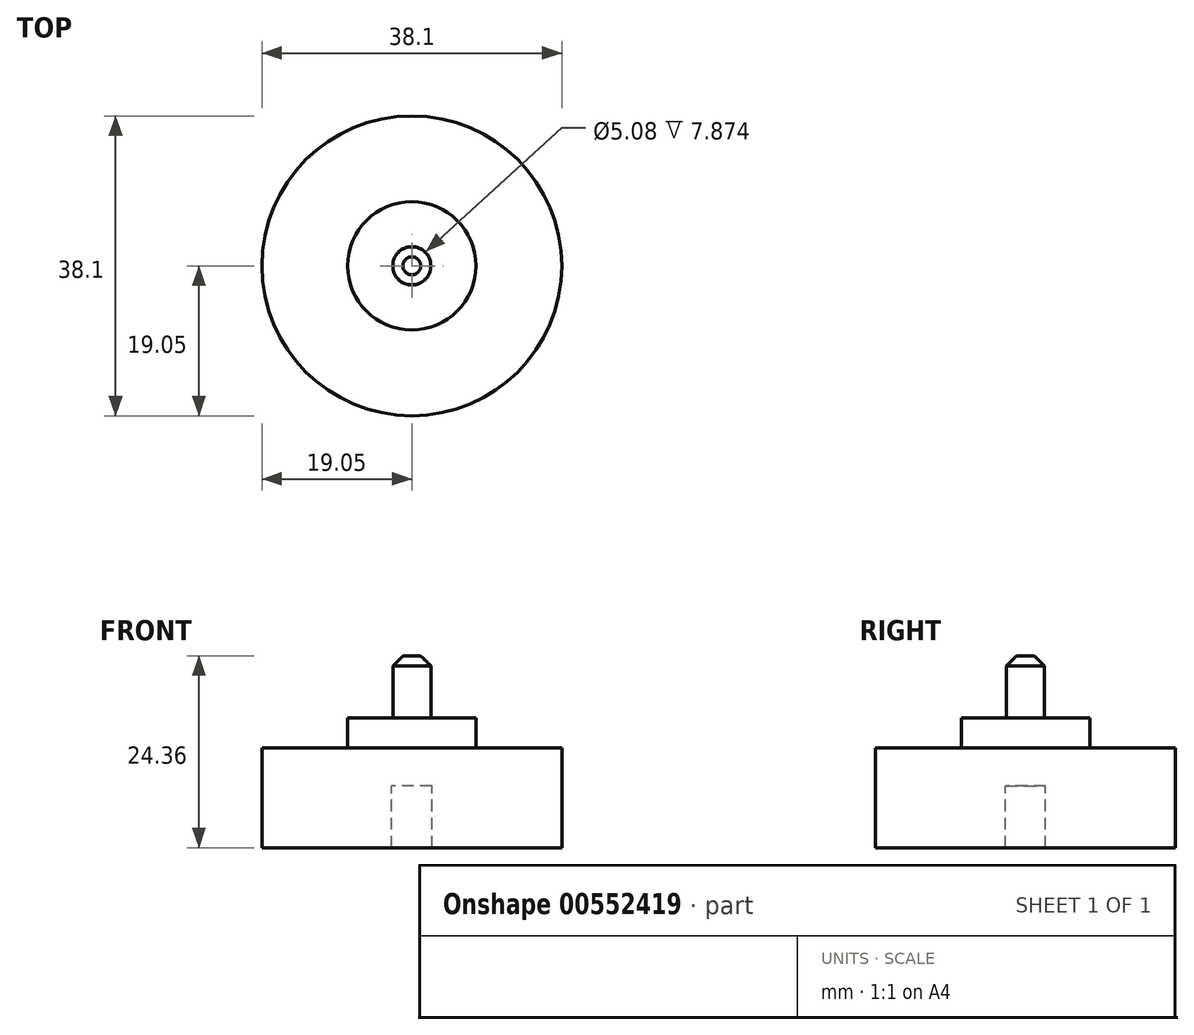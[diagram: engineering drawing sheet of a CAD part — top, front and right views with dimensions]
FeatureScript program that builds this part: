
annotation { "Feature Type Name" : "Feature", "Feature Type Description" : "" }
export const myFeature = defineFeature(function(context is Context, id is Id, definition is map)
    precondition{}
    {
        {
            var Q0;
            Q0=qCreatedBy(makeId("Front.planeOp"),FACE);
            var sketch = newSketch(context, id + "F0", { "sketchPlane" : qUnion([Q0])});
            skLineSegment(sketch, "E0", {"start": v(19.05, 0) * mm, "end": v(19.05, 12.7) * mm});
            skLineSegment(sketch, "E1", {"start": v(2.54, 0) * mm, "end": v(2.54, 7.87) * mm});
            skLineSegment(sketch, "E2", {"start": v(2.54, 7.87) * mm, "end": v(0, 7.87) * mm});
            skPoint(sketch, "E3.start.orphan", {"position": v(0, 12.7) * mm});
            skLineSegment(sketch, "E4", {"start": v(2.54, 0) * mm, "end": v(19.05, 0) * mm});
            skLineSegment(sketch, "E5", {"start": v(0, 16.51) * mm, "end": v(0, 7.87) * mm});
            skLineSegment(sketch, "E6", {"start": v(19.05, 12.7) * mm, "end": v(8.15, 12.7) * mm});
            skLineSegment(sketch, "E7", {"start": v(2.41, 16.51) * mm, "end": v(8.15, 16.51) * mm});
            skLineSegment(sketch, "E8", {"start": v(8.15, 16.51) * mm, "end": v(8.15, 12.7) * mm});
            skPoint(sketch, "E9.orphan", {"position": v(0, 25.15) * mm});
            skLineSegment(sketch, "E10", {"start": v(0, 16.51) * mm, "end": v(0, 24.36) * mm});
            skLineSegment(sketch, "E11", {"start": v(0, 24.36) * mm, "end": v(2.41, 24.36) * mm});
            skLineSegment(sketch, "E12", {"start": v(2.41, 24.36) * mm, "end": v(2.41, 16.51) * mm});
            skSolve(sketch);
        }
        {
            var Q0;
            Q0 = qSketchRegion(id + "F0", true);
            var Q1;
            Q1=sQuery(id+"F0.wireOp",EDGE,"E5");
            revolve(context, id + "F1", {"entities" : qUnion([Q0]), "axis" : qUnion([Q1]), "revolveType" : RevolveType.FULL});
        }
        {
            var Q0;
            Q0=makeQuery(id+"F1.opRevolve","SWEPT_EDGE",EDGE,{"disambiguationData":[OSD([sQuery(id+"F0.wireOp",EDGE,"E11"),sQuery(id+"F0.wireOp",EDGE,"E12")])]});
            chamfer(context, id + "F2", {"entities" : qUnion([Q0]), "width" : 1.27 * mm, "tangentPropagation" : true});
        }
    });
